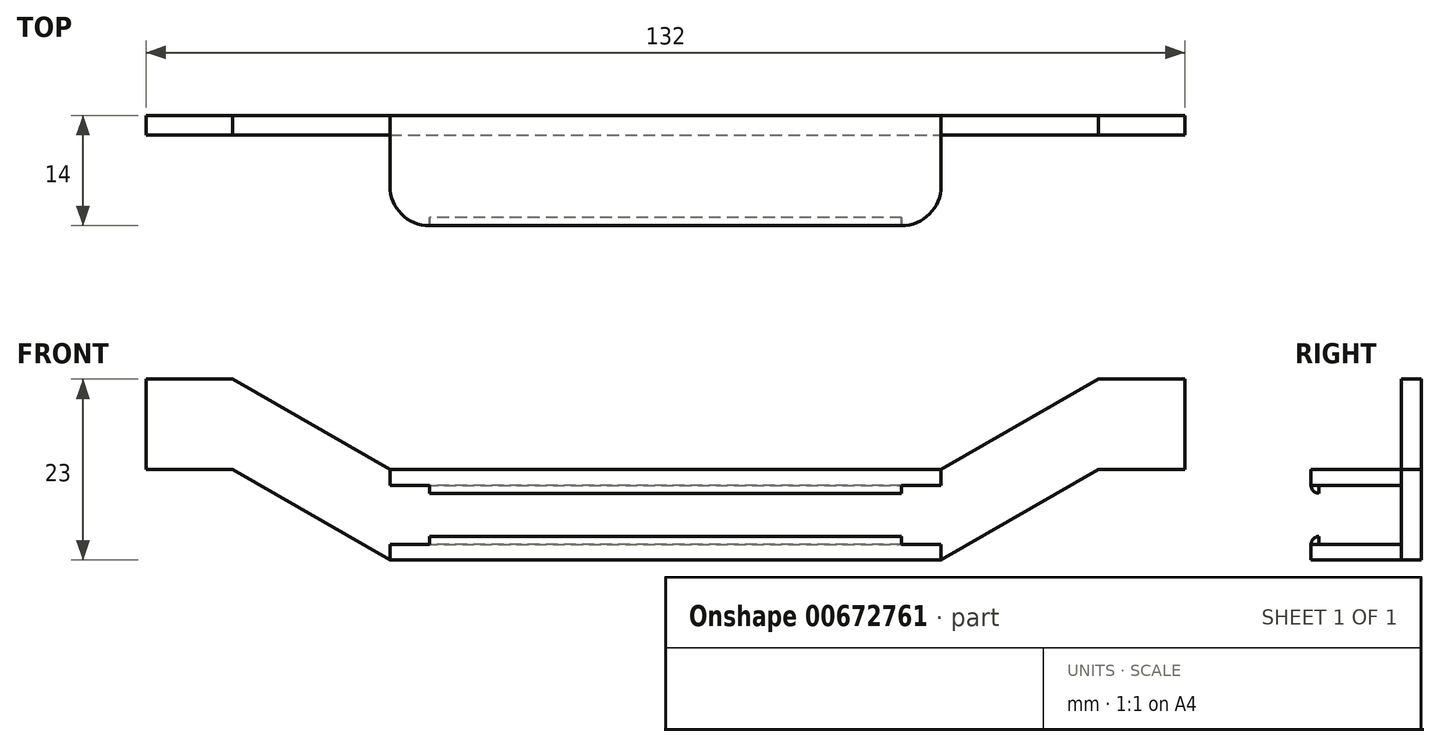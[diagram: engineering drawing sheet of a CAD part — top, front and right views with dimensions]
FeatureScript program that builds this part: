
annotation { "Feature Type Name" : "Feature", "Feature Type Description" : "" }
export const myFeature = defineFeature(function(context is Context, id is Id, definition is map)
    precondition{}
    {
        {
            var Q0;
            Q0=qCreatedBy(makeId("Front.planeOp"),FACE);
            var sketch = newSketch(context, id + "F0", { "sketchPlane" : qUnion([Q0])});
            skLineSegment(sketch, "E0.bottom", {"start": v(-66, 23) * mm, "end": v(-55, 23) * mm});
            skLineSegment(sketch, "E0.left", {"start": v(-66, 23) * mm, "end": v(-66, 11.5) * mm});
            skLineSegment(sketch, "E0.right", {"start": v(66, 23) * mm, "end": v(66, 11.5) * mm});
            skLineSegment(sketch, "E1.bottom", {"start": v(-35, 0) * mm, "end": v(35, 0) * mm});
            skLineSegment(sketch, "E1.top", {"start": v(-35, 11.5) * mm, "end": v(35, 11.5) * mm});
            skLineSegment(sketch, "E1.left", {"start": v(-35, 0) * mm, "end": v(-35, 11.5) * mm});
            skLineSegment(sketch, "E1.right", {"start": v(35, 0) * mm, "end": v(35, 11.5) * mm});
            skLineSegment(sketch, "E2", {"start": v(-35, 9.5) * mm, "end": v(35, 9.5) * mm});
            skLineSegment(sketch, "E3", {"start": v(-35, 2) * mm, "end": v(35, 2) * mm});
            skLineSegment(sketch, "E4", {"start": v(-35, 11.5) * mm, "end": v(-55, 23) * mm});
            skLineSegment(sketch, "E5", {"start": v(-75, 11.5) * mm, "end": v(-75, 24.95) * mm});
            skLineSegment(sketch, "E6", {"start": v(-75, 24.95) * mm, "end": v(75, 24.95) * mm});
            skLineSegment(sketch, "E7", {"start": v(75, 24.95) * mm, "end": v(75, 11.5) * mm});
            skLineSegment(sketch, "E8", {"start": v(-66, 11.5) * mm, "end": v(-55, 11.5) * mm});
            skLineSegment(sketch, "E9", {"start": v(55, 11.5) * mm, "end": v(66, 11.5) * mm});
            skLineSegment(sketch, "E10", {"start": v(35, 11.5) * mm, "end": v(55, 23) * mm});
            skLineSegment(sketch, "E11", {"start": v(35, 0) * mm, "end": v(55, 11.5) * mm});
            skLineSegment(sketch, "E12", {"start": v(-35, 0) * mm, "end": v(-55, 11.5) * mm});
            skLineSegment(sketch, "E13.trimOffspring", {"start": v(55, 23) * mm, "end": v(66, 23) * mm});
            skPoint(sketch, "E14.trimOffspring.start.orphan", {"position": v(55, 0) * mm});
            skPoint(sketch, "E0.top.end.orphan", {"position": v(-55, 0) * mm});
            skLineSegment(sketch, "E15", {"start": v(-66, 11.5) * mm, "end": v(-75, 11.5) * mm});
            skLineSegment(sketch, "E16", {"start": v(66, 11.5) * mm, "end": v(75, 11.5) * mm});
            skPoint(sketch, "E17.start.orphan", {"position": v(-66, 0) * mm});
            skPoint(sketch, "E18.orphan", {"position": v(-75, 0) * mm});
            skPoint(sketch, "E19.end.orphan", {"position": v(66, 0) * mm});
            skPoint(sketch, "E19.start.orphan", {"position": v(75, 0) * mm});
            skSolve(sketch);
        }
        {
            var Q0;
            Q0=makeQuery(id+"F0.imprint","IMPRINT",FACE,{"disambiguationData":[TD([[makeQuery(id+"F0.imprint","IMPRINT",EDGE,{"derivedFrom":sQuery(id+"F0.wireOp",EDGE,"E0.bottom")}),-1.0]])]});
            var Q1;
            Q1=makeQuery(id+"F0.imprint","IMPRINT",FACE,{"disambiguationData":[TD([[makeQuery(id+"F0.imprint","IMPRINT",EDGE,{"derivedFrom":sQuery(id+"F0.wireOp",EDGE,"E0.right")}),-1.0]])]});
            var Q2;
            {var subQ0=sQuery(id+"F0.wireOp",EDGE,"E2");Q2=makeQuery(id+"F0.imprint","IMPRINT",FACE,{"disambiguationData":[TD([[makeQuery(id+"F0.imprint","IMPRINT",EDGE,{"derivedFrom":subQ0}),-1.0]])]});}
            extrude(context, id + "F1", {"entities" : qUnion([Q0, Q1, Q2]), "depth" : 2.5 * mm, "offsetDistance" : 2.5 * mm});
        }
        {
            var Q0;
            {var subQ0=sQuery(id+"F0.wireOp",EDGE,"E1.top");Q0=makeQuery(id+"F0.imprint","IMPRINT",FACE,{"disambiguationData":[TD([[makeQuery(id+"F0.imprint","IMPRINT",EDGE,{"derivedFrom":subQ0}),-1.0]])]});}
            var Q1;
            {var subQ2=sQuery(id+"F0.wireOp",EDGE,"E3");Q1=makeQuery(id+"F0.imprint","IMPRINT",FACE,{"disambiguationData":[TD([[makeQuery(id+"F0.imprint","IMPRINT",EDGE,{"derivedFrom":subQ2}),-1.0]])]});}
            extrude(context, id + "F2", {"entities" : qUnion([Q0, Q1]), "operationType" : NewBodyOperationType.ADD, "depth" : 14 * mm, "offsetDistance" : 25 * mm});
        }
        {
            var Q0;
            Q0=qCreatedBy(makeId("Right.planeOp"),FACE);
            var sketch = newSketch(context, id + "F3", { "sketchPlane" : qUnion([Q0])});
            skArc(sketch, "E20", {"start": v(-14, 9.5) * mm, "mid": v(-13.7, 8.8) * mm, "end": v(-13, 8.5) * mm});
            skLineSegment(sketch, "E21", {"start": v(-13, 9.5) * mm, "end": v(-13, 8.5) * mm});
            skLineSegment(sketch, "E22", {"start": v(-13, 9.5) * mm, "end": v(-14, 9.5) * mm});
            skArc(sketch, "E23", {"start": v(-13, 3) * mm, "mid": v(-13.7, 2.7) * mm, "end": v(-14, 2) * mm});
            skLineSegment(sketch, "E24", {"start": v(-13, 3) * mm, "end": v(-13, 2) * mm});
            skLineSegment(sketch, "E25", {"start": v(-13, 2) * mm, "end": v(-14, 2) * mm});
            skSolve(sketch);
        }
        {
            var Q0;
            Q0=makeQuery(id+"F3.imprint","IMPRINT",FACE,{"disambiguationData":[TD([[makeQuery(id+"F3.imprint","IMPRINT",EDGE,{"derivedFrom":sQuery(id+"F3.wireOp",EDGE,"E20")}),1.0]])]});
            var Q1;
            Q1=makeQuery(id+"F3.imprint","IMPRINT",FACE,{"disambiguationData":[TD([[makeQuery(id+"F3.imprint","IMPRINT",EDGE,{"derivedFrom":sQuery(id+"F3.wireOp",EDGE,"E23")}),1.0]])]});
            extrude(context, id + "F4", {"entities" : qUnion([Q0, Q1]), "operationType" : NewBodyOperationType.ADD, "endBound" : BoundingType.SYMMETRIC, "depth" : 60 * mm, "offsetDistance" : 25 * mm});
        }
        {
            var Q0;
            {var subQ0=sQuery(id+"F0.wireOp",EDGE,"E1.right");Q0=makeQuery(id+"F2.opExtrude","CAP_EDGE",EDGE,{"disambiguationData":[OSD([subQ0]),TDD([makeQuery(id+"F0.imprint","IMPRINT",EDGE,{"disambiguationData":[TD([[makeQuery(id+"F0.imprint","INTERSECT",VERTEX,{"derivedFrom":[subQ0,sQuery(id+"F0.wireOp",EDGE,"E2")]}),-1.0]])],"derivedFrom":subQ0})])],"isStart":false});}
            var Q1;
            {var subQ0=sQuery(id+"F0.wireOp",EDGE,"E1.right");Q1=makeQuery(id+"F2.opExtrude","CAP_EDGE",EDGE,{"disambiguationData":[OSD([subQ0]),TDD([makeQuery(id+"F0.imprint","IMPRINT",EDGE,{"disambiguationData":[TD([[makeQuery(id+"F0.imprint","INTERSECT",VERTEX,{"derivedFrom":[subQ0,sQuery(id+"F0.wireOp",EDGE,"E3")]}),1.0]])],"derivedFrom":subQ0})])],"isStart":false});}
            var Q2;
            {var subQ0=sQuery(id+"F0.wireOp",EDGE,"E1.left");Q2=makeQuery(id+"F2.opExtrude","CAP_EDGE",EDGE,{"disambiguationData":[OSD([subQ0]),TDD([makeQuery(id+"F0.imprint","IMPRINT",EDGE,{"disambiguationData":[TD([[makeQuery(id+"F0.imprint","INTERSECT",VERTEX,{"derivedFrom":[subQ0,sQuery(id+"F0.wireOp",EDGE,"E3")]}),1.0]])],"derivedFrom":subQ0})])],"isStart":false});}
            var Q3;
            {var subQ0=sQuery(id+"F0.wireOp",EDGE,"E1.left");Q3=makeQuery(id+"F2.opExtrude","CAP_EDGE",EDGE,{"disambiguationData":[OSD([subQ0]),TDD([makeQuery(id+"F0.imprint","IMPRINT",EDGE,{"disambiguationData":[TD([[makeQuery(id+"F0.imprint","INTERSECT",VERTEX,{"derivedFrom":[subQ0,sQuery(id+"F0.wireOp",EDGE,"E2")]}),-1.0]])],"derivedFrom":subQ0})])],"isStart":false});}
            fillet(context, id + "F5", {"entities" : qUnion([Q0, Q1, Q2, Q3]), "radius" : 5 * mm, "tangentPropagation" : true, "allowEdgeOverflow" : false});
        }
    });
